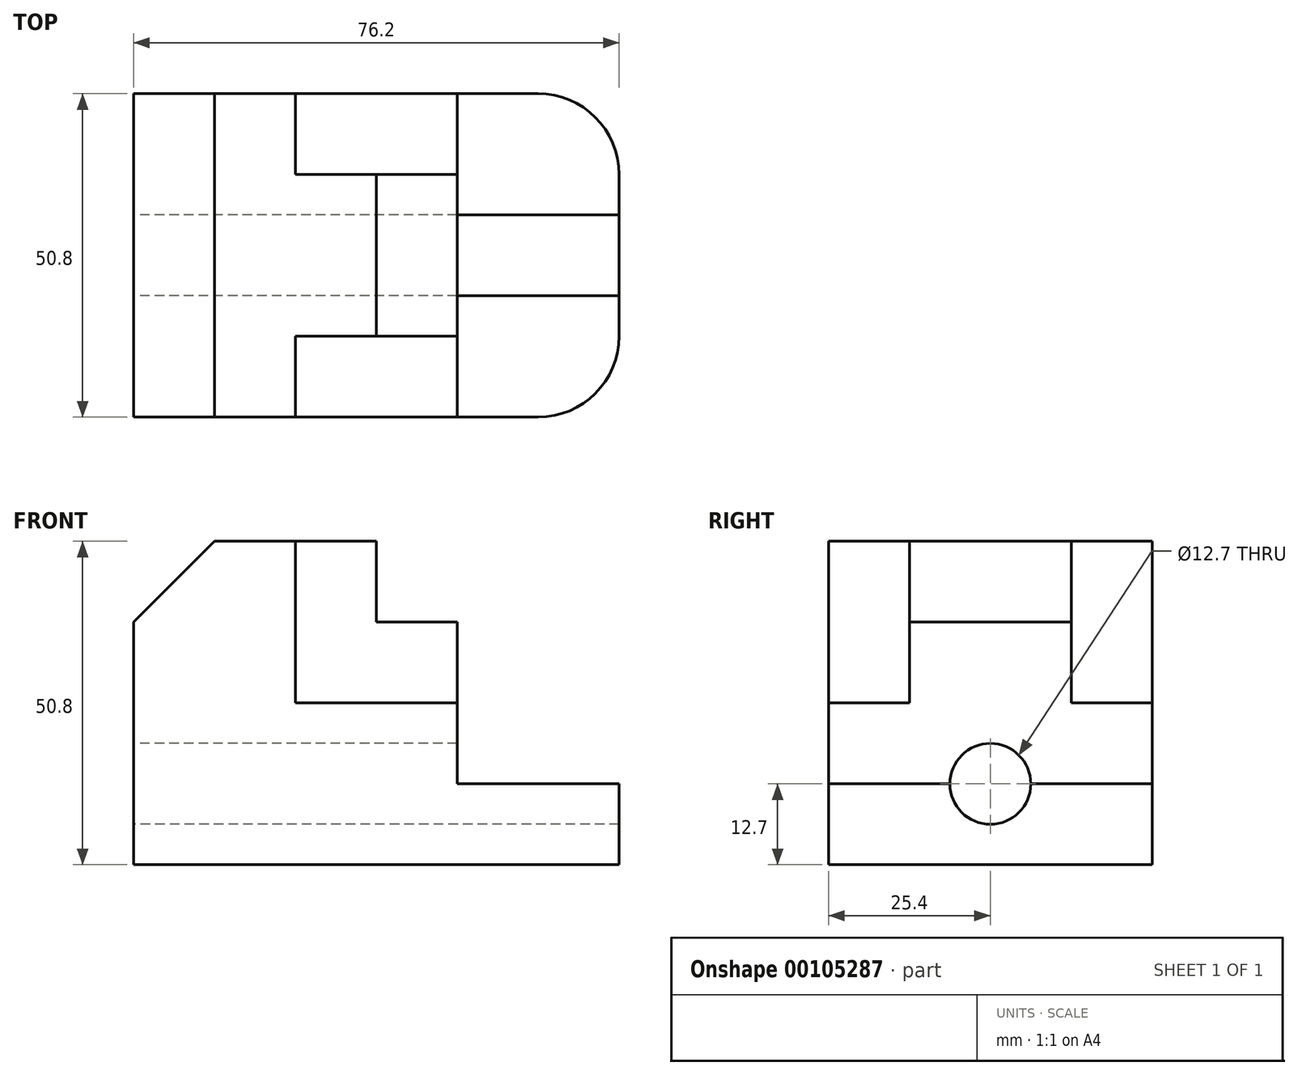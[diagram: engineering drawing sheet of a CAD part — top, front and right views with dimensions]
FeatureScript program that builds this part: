
annotation { "Feature Type Name" : "Feature", "Feature Type Description" : "" }
export const myFeature = defineFeature(function(context is Context, id is Id, definition is map)
    precondition{}
    {
        {
            var Q0;
            Q0=qCreatedBy(makeId("Front.planeOp"),FACE);
            var sketch = newSketch(context, id + "F0", { "sketchPlane" : qUnion([Q0])});
            skLineSegment(sketch, "E0", {"start": v(0, 0) * mm, "end": v(76.2, 0) * mm});
            skLineSegment(sketch, "E1", {"start": v(76.2, 0) * mm, "end": v(76.2, 12.7) * mm});
            skLineSegment(sketch, "E2", {"start": v(76.2, 12.7) * mm, "end": v(50.8, 12.7) * mm});
            skLineSegment(sketch, "E3", {"start": v(50.8, 12.7) * mm, "end": v(50.8, 25.4) * mm});
            skLineSegment(sketch, "E4", {"start": v(50.8, 25.4) * mm, "end": v(25.4, 25.4) * mm});
            skLineSegment(sketch, "E5", {"start": v(25.4, 25.4) * mm, "end": v(25.4, 50.8) * mm});
            skLineSegment(sketch, "E6", {"start": v(0, 38.1) * mm, "end": v(0, 0) * mm});
            skLineSegment(sketch, "E7", {"start": v(25.4, 50.8) * mm, "end": v(38.1, 50.8) * mm});
            skLineSegment(sketch, "E8", {"start": v(38.1, 50.8) * mm, "end": v(38.1, 38.1) * mm});
            skLineSegment(sketch, "E9", {"start": v(38.1, 38.1) * mm, "end": v(50.8, 38.1) * mm});
            skLineSegment(sketch, "E10", {"start": v(50.8, 38.1) * mm, "end": v(50.8, 25.4) * mm});
            skLineSegment(sketch, "E11", {"start": v(25.4, 50.8) * mm, "end": v(12.7, 50.8) * mm});
            skLineSegment(sketch, "E12", {"start": v(0, 38.1) * mm, "end": v(12.7, 50.8) * mm});
            skSolve(sketch);
        }
        {
            var Q0;
            Q0=makeQuery(id+"F0.imprint","IMPRINT",FACE,{"disambiguationData":[TD([[makeQuery(id+"F0.imprint","IMPRINT",EDGE,{"derivedFrom":sQuery(id+"F0.wireOp",EDGE,"E0")}),1.0]])]});
            extrude(context, id + "F1", {"entities" : qUnion([Q0]), "oppositeDirection" : true, "depth" : 50.8 * mm});
        }
        {
            var Q0;
            Q0=makeQuery(id+"F0.imprint","IMPRINT",FACE,{"disambiguationData":[TD([[makeQuery(id+"F0.imprint","IMPRINT",EDGE,{"derivedFrom":sQuery(id+"F0.wireOp",EDGE,"E4")}),-1.0]])]});
            extrude(context, id + "F2", {"entities" : qUnion([Q0]), "operationType" : NewBodyOperationType.ADD, "oppositeDirection" : true, "depth" : 50.8 * mm});
        }
        {
            var Q0;
            Q0=makeQuery(id+"F2.boolean.opBoolean","MERGE",FACE,{"derivedFrom":[makeQuery(id+"F1.opExtrude","SWEPT_FACE",FACE,{"disambiguationData":[OSD([sQuery(id+"F0.wireOp",EDGE,"E11")])]}),makeQuery(id+"F2.opExtrude","SWEPT_FACE",FACE,{"disambiguationData":[OSD([sQuery(id+"F0.wireOp",EDGE,"E7")])]})]});
            var sketch = newSketch(context, id + "F3", { "sketchPlane" : qUnion([Q0])});
            skLineSegment(sketch, "E13", {"start": v(25.4, 0) * mm, "end": v(25.4, 12.7) * mm});
            skLineSegment(sketch, "E14", {"start": v(25.4, 12.7) * mm, "end": v(38.1, 12.7) * mm});
            skLineSegment(sketch, "E15", {"start": v(38.1, 12.7) * mm, "end": v(38.1, 0) * mm});
            skLineSegment(sketch, "E16", {"start": v(38.1, 0) * mm, "end": v(25.4, 0) * mm});
            skSolve(sketch);
        }
        {
            var Q0;
            Q0=makeQuery(id+"F3.imprint","IMPRINT",FACE,{"disambiguationData":[TD([[makeQuery(id+"F3.imprint","IMPRINT",EDGE,{"derivedFrom":sQuery(id+"F3.wireOp",EDGE,"E13")}),-1.0]])]});
            extrude(context, id + "F4", {"entities" : qUnion([Q0]), "operationType" : NewBodyOperationType.REMOVE, "oppositeDirection" : true, "depth" : 25.4 * mm});
        }
        {
            var Q0;
            Q0=makeQuery(id+"F2.boolean.opBoolean","MERGE",FACE,{"derivedFrom":[makeQuery(id+"F1.opExtrude","SWEPT_FACE",FACE,{"disambiguationData":[OSD([sQuery(id+"F0.wireOp",EDGE,"E11")])]}),makeQuery(id+"F2.opExtrude","SWEPT_FACE",FACE,{"disambiguationData":[OSD([sQuery(id+"F0.wireOp",EDGE,"E7")])]})]});
            var sketch = newSketch(context, id + "F5", { "sketchPlane" : qUnion([Q0])});
            skLineSegment(sketch, "E17", {"start": v(38.1, 50.8) * mm, "end": v(25.4, 50.8) * mm});
            skLineSegment(sketch, "E18", {"start": v(25.4, 50.8) * mm, "end": v(25.4, 38.1) * mm});
            skLineSegment(sketch, "E19", {"start": v(25.4, 38.1) * mm, "end": v(38.1, 38.1) * mm});
            skLineSegment(sketch, "E20", {"start": v(38.1, 38.1) * mm, "end": v(38.1, 50.8) * mm});
            skSolve(sketch);
        }
        {
            var Q0;
            Q0=makeQuery(id+"F5.imprint","IMPRINT",FACE,{"disambiguationData":[TD([[makeQuery(id+"F5.imprint","IMPRINT",EDGE,{"derivedFrom":sQuery(id+"F5.wireOp",EDGE,"E17")}),1.0]])]});
            extrude(context, id + "F6", {"entities" : qUnion([Q0]), "operationType" : NewBodyOperationType.REMOVE, "oppositeDirection" : true, "depth" : 25.4 * mm});
        }
        {
            var Q0;
            Q0=makeQuery(id+"F2.opExtrude","SWEPT_FACE",FACE,{"disambiguationData":[OSD([sQuery(id+"F0.wireOp",EDGE,"E9")])]});
            var sketch = newSketch(context, id + "F7", { "sketchPlane" : qUnion([Q0])});
            skLineSegment(sketch, "E21", {"start": v(38.1, 0) * mm, "end": v(38.1, 12.7) * mm});
            skLineSegment(sketch, "E22", {"start": v(38.1, 12.7) * mm, "end": v(50.8, 12.7) * mm});
            skLineSegment(sketch, "E23", {"start": v(50.8, 12.7) * mm, "end": v(50.8, 0) * mm});
            skLineSegment(sketch, "E24", {"start": v(50.8, 0) * mm, "end": v(38.1, 0) * mm});
            skLineSegment(sketch, "E25", {"start": v(38.1, 50.8) * mm, "end": v(38.1, 38.1) * mm});
            skLineSegment(sketch, "E26", {"start": v(38.1, 38.1) * mm, "end": v(50.8, 38.1) * mm});
            skLineSegment(sketch, "E27", {"start": v(50.8, 38.1) * mm, "end": v(50.8, 50.8) * mm});
            skLineSegment(sketch, "E28", {"start": v(38.1, 50.8) * mm, "end": v(50.8, 50.8) * mm});
            skSolve(sketch);
        }
        {
            var Q0;
            Q0=makeQuery(id+"F7.imprint","IMPRINT",FACE,{"disambiguationData":[TD([[makeQuery(id+"F7.imprint","IMPRINT",EDGE,{"derivedFrom":sQuery(id+"F7.wireOp",EDGE,"E21")}),1.0]])]});
            var Q1;
            Q1=makeQuery(id+"F7.imprint","IMPRINT",FACE,{"disambiguationData":[TD([[makeQuery(id+"F7.imprint","IMPRINT",EDGE,{"derivedFrom":sQuery(id+"F7.wireOp",EDGE,"E25")}),1.0]])]});
            extrude(context, id + "F8", {"entities" : qUnion([Q0, Q1]), "operationType" : NewBodyOperationType.REMOVE, "oppositeDirection" : true, "depth" : 12.7 * mm});
        }
        {
            var Q0;
            Q0=makeQuery(id+"F1.opExtrude","CAP_EDGE",EDGE,{"disambiguationData":[OSD([sQuery(id+"F0.wireOp",EDGE,"E1")])],"isStart":true});
            var Q1;
            Q1=makeQuery(id+"F1.opExtrude","CAP_EDGE",EDGE,{"disambiguationData":[OSD([sQuery(id+"F0.wireOp",EDGE,"E1")])],"isStart":false});
            fillet(context, id + "F9", {"entities" : qUnion([Q0, Q1]), "radius" : 12.7 * mm, "tangentPropagation" : true, "allowEdgeOverflow" : false});
        }
        {
            var Q0;
            Q0=makeQuery(id+"F2.boolean.opBoolean","MERGE",FACE,{"derivedFrom":[makeQuery(id+"F1.opExtrude","SWEPT_FACE",FACE,{"disambiguationData":[OSD([sQuery(id+"F0.wireOp",EDGE,"E3")])]}),makeQuery(id+"F2.opExtrude","SWEPT_FACE",FACE,{"disambiguationData":[OSD([sQuery(id+"F0.wireOp",EDGE,"E10")])]})]});
            var sketch = newSketch(context, id + "F10", { "sketchPlane" : qUnion([Q0])});
            skCircle(sketch, "E29", {"center": v(25.4, 12.7) * mm, "radius": 6.35 * mm});
            skSolve(sketch);
        }
        {
            var Q0;
            {var subQ0=sQuery(id+"F10.wireOp",EDGE,"E29");var subQ1=makeQuery(id+"F1.opExtrude","SWEPT_EDGE",EDGE,{"disambiguationData":[OSD([sQuery(id+"F0.wireOp",EDGE,"E2"),sQuery(id+"F0.wireOp",EDGE,"E3")])]});var subQ2=makeQuery(id+"F10.imprint","INTERSECT",VERTEX,{"disambiguationData":[OD(0.0)],"derivedFrom":[subQ1,subQ0]});Q0=makeQuery(id+"F10.imprint","IMPRINT",FACE,{"disambiguationData":[TD([[makeQuery(id+"F10.imprint","IMPRINT",EDGE,{"disambiguationData":[TD([[subQ2,-1.0]])],"derivedFrom":subQ0}),1.0]])]});}
            var Q1;
            {var subQ0=sQuery(id+"F10.wireOp",EDGE,"E29");var subQ1=makeQuery(id+"F1.opExtrude","SWEPT_EDGE",EDGE,{"disambiguationData":[OSD([sQuery(id+"F0.wireOp",EDGE,"E2"),sQuery(id+"F0.wireOp",EDGE,"E3")])]});var subQ2=makeQuery(id+"F10.imprint","INTERSECT",VERTEX,{"disambiguationData":[OD(0.0)],"derivedFrom":[subQ1,subQ0]});Q1=makeQuery(id+"F10.imprint","IMPRINT",FACE,{"disambiguationData":[TD([[makeQuery(id+"F10.imprint","IMPRINT",EDGE,{"disambiguationData":[TD([[subQ2,1.0]])],"derivedFrom":subQ0}),1.0]])]});}
            extrude(context, id + "F11", {"entities" : qUnion([Q0, Q1]), "operationType" : NewBodyOperationType.REMOVE, "endBound" : BoundingType.SYMMETRIC, "depth" : 259.12 * mm});
        }
    });
